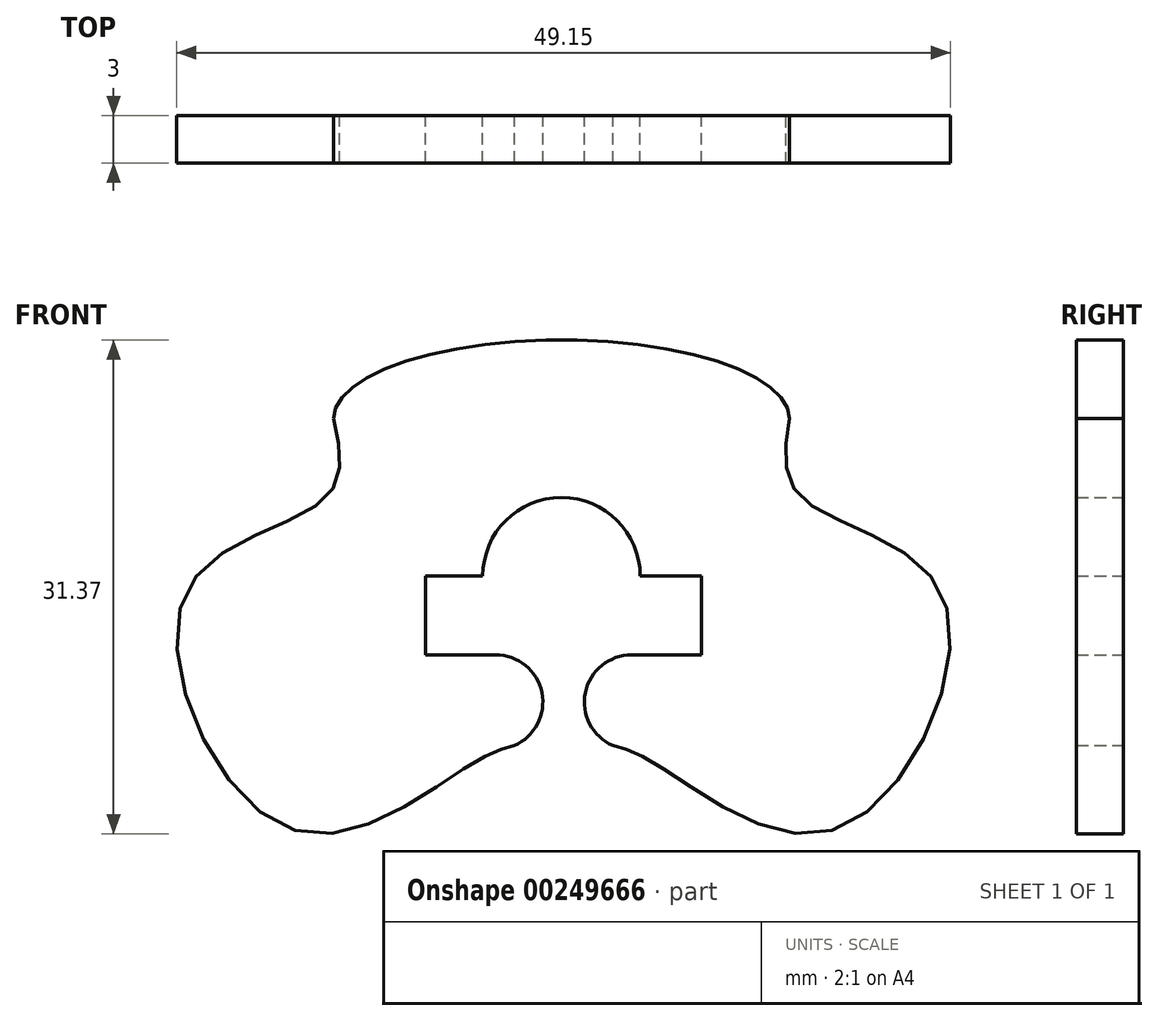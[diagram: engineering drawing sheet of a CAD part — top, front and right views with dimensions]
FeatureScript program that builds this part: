
annotation { "Feature Type Name" : "Feature", "Feature Type Description" : "" }
export const myFeature = defineFeature(function(context is Context, id is Id, definition is map)
    precondition{}
    {
        {
            var Q0;
            Q0=qCreatedBy(makeId("Front.planeOp"),FACE);
            var sketch = newSketch(context, id + "F0", { "sketchPlane" : qUnion([Q0])});
            skLineSegment(sketch, "E0", {"start": v(-8.75, -5.88) * mm, "end": v(-8.75, -0.88) * mm});
            skLineSegment(sketch, "E1", {"start": v(8.76, -5.88) * mm, "end": v(8.76, -0.88) * mm});
            skLineSegment(sketch, "E2", {"start": v(-8.75, -0.88) * mm, "end": v(-5.13, -0.88) * mm});
            skLineSegment(sketch, "E3", {"start": v(4.87, -0.88) * mm, "end": v(8.76, -0.88) * mm});
            skLineSegment(sketch, "E4", {"start": v(8.76, -5.88) * mm, "end": v(4.32, -5.88) * mm});
            skFitSpline(sketch, "E5", {"points": [v(14.34, 9.12) * mm, v(15.1, 4.11) * mm, v(24.08, -2.1) * mm, v(17.27, -16.95) * mm, v(5.88, -12.82) * mm, v(3.13, -11.64) * mm]});
            skArc(sketch, "E6", {"start": v(4.32, -5.88) * mm, "mid": v(1.38, -8.28) * mm, "end": v(3.13, -11.64) * mm});
            skLineSegment(sketch, "E7", {"start": v(-8.75, -5.88) * mm, "end": v(-4.32, -5.88) * mm});
            skFitSpline(sketch, "E8", {"points": [v(-14.6, 9.12) * mm, v(-15.1, 4.11) * mm, v(-24.08, -2.1) * mm, v(-17.27, -16.95) * mm, v(-5.88, -12.82) * mm, v(-3.13, -11.64) * mm]});
            skArc(sketch, "E9", {"start": v(-3.13, -11.64) * mm, "mid": v(-1.38, -8.28) * mm, "end": v(-4.32, -5.88) * mm});
            skEllipticalArc(sketch, "E10", {});
            skArc(sketch, "E11", {"start": v(4.87, -0.88) * mm, "mid": v(-0.13, 4.12) * mm, "end": v(-5.13, -0.88) * mm});
            const initialGuessF0  = {"E10": [-0.00013403900000002978, 0.009117351999999983, 14.475796, 0, 0.014475796, 0.005, 0, 3.141593]};
            skSetInitialGuess(sketch, initialGuessF0);
            skSolve(sketch);
        }
        {
            var Q0;
            Q0=makeQuery(id+"F0.imprint","IMPRINT",FACE,{"disambiguationData":[TD([[makeQuery(id+"F0.imprint","IMPRINT",EDGE,{"derivedFrom":sQuery(id+"F0.wireOp",EDGE,"E0")}),1.0]])]});
            extrude(context, id + "F1", {"entities" : qUnion([Q0]), "depth" : 3 * mm});
        }
    });
